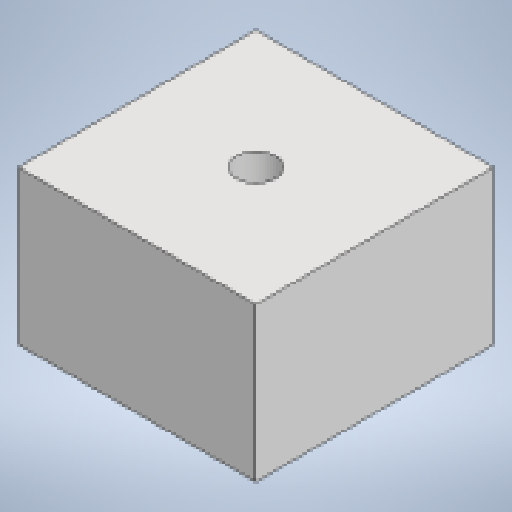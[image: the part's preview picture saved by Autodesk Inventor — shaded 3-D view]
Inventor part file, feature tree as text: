
AUTODESK INVENTOR PART (.ipt)
format: ipt  version: 2025.1 (Build 291241020, 241B)  size: 134,144 bytes
history: native  units: mm
features: extrude x2, sketch x2, projected_geometry x1
ambient origin geometry x8: Origin, YZ Plane, XZ Plane, XY Plane, X Axis, Y Axis, Z Axis, Center Point
bodies: Solid1 (feature_tree)
feature tree (5):
  extrude  "Extrusion1"  Depth=170.0mm
  extrude  "Extrusion2"  Depth=110.0mm TaperAngle=0.0deg
  sketch  "Sketch1"  dims[d0=170.0mm d1=170.0mm]
  sketch  "Sketch2"  dims[d2=28.0mm d3=110.0mm d4=0.0mm d5=271.0mm d6=0.0mm]
  projected_geometry  "Projected Loop1"
